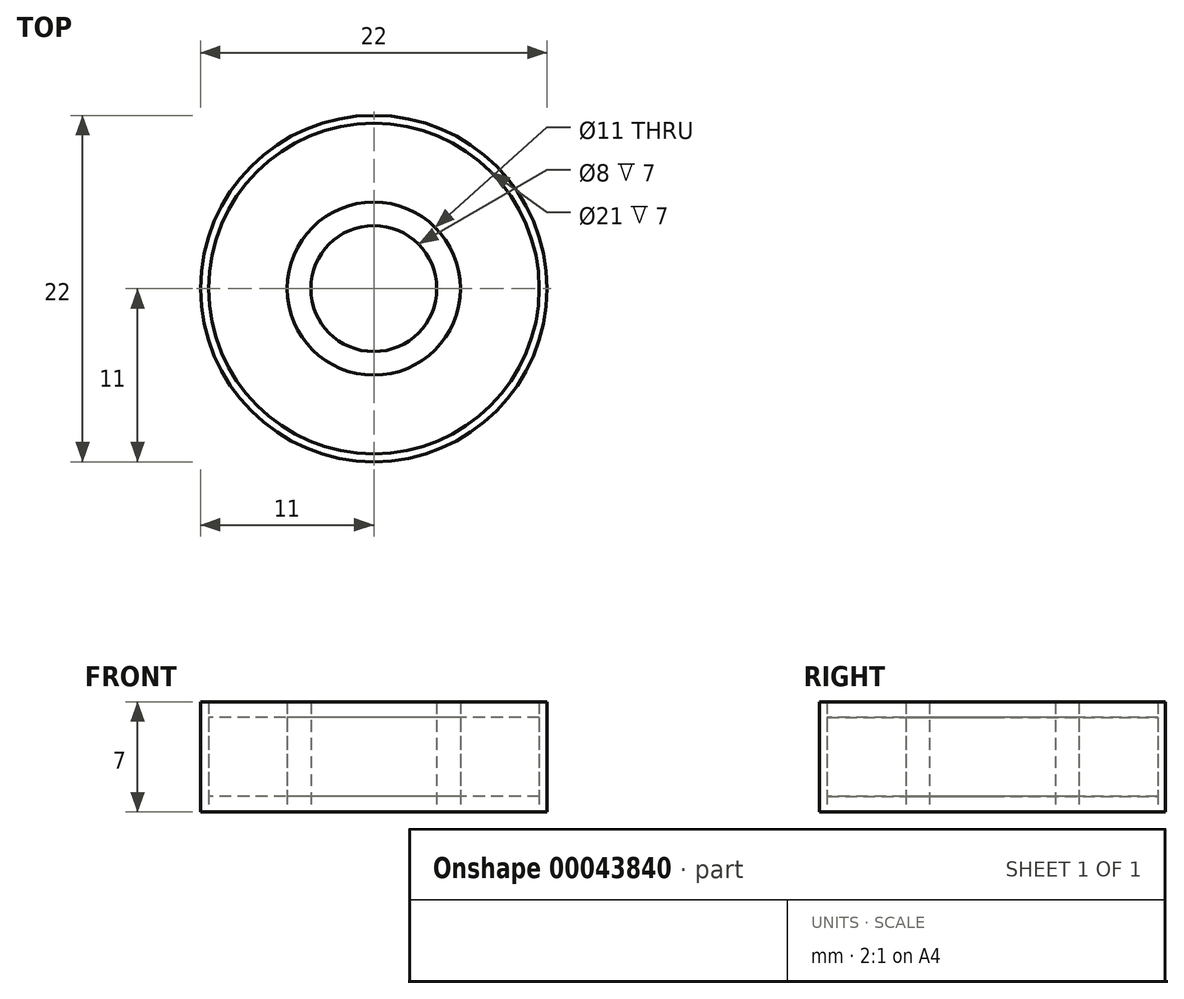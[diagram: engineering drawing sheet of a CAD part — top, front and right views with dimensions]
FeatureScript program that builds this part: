
annotation { "Feature Type Name" : "Feature", "Feature Type Description" : "" }
export const myFeature = defineFeature(function(context is Context, id is Id, definition is map)
    precondition{}
    {
        {
            var Q0;
            Q0=qCreatedBy(makeId("Top.planeOp"),FACE);
            var sketch = newSketch(context, id + "F0", { "sketchPlane" : qUnion([Q0])});
            skCircle(sketch, "E0", {"center": v(0, 0) * mm, "radius": 4 * mm});
            skCircle(sketch, "E1", {"center": v(0, 0) * mm, "radius": 11 * mm});
            skCircle(sketch, "E2", {"center": v(0, 0) * mm, "radius": 5.5 * mm});
            skCircle(sketch, "E3", {"center": v(0, 0) * mm, "radius": 10.5 * mm});
            skSolve(sketch);
        }
        {
            var Q0;
            Q0=makeQuery(id+"F0.imprint","IMPRINT",FACE,{"disambiguationData":[TD([[makeQuery(id+"F0.imprint","IMPRINT",EDGE,{"derivedFrom":sQuery(id+"F0.wireOp",EDGE,"E0")}),-1.0]])]});
            var Q1;
            Q1=makeQuery(id+"F0.imprint","IMPRINT",FACE,{"disambiguationData":[TD([[makeQuery(id+"F0.imprint","IMPRINT",EDGE,{"derivedFrom":sQuery(id+"F0.wireOp",EDGE,"E1")}),1.0]])]});
            extrude(context, id + "F1", {"entities" : qUnion([Q0, Q1]), "depth" : 7 * mm});
        }
        {
            var Q0;
            Q0=makeQuery(id+"F0.imprint","IMPRINT",FACE,{"disambiguationData":[TD([[makeQuery(id+"F0.imprint","IMPRINT",EDGE,{"derivedFrom":sQuery(id+"F0.wireOp",EDGE,"E2")}),-1.0]])]});
            extrude(context, id + "F2", {"entities" : qUnion([Q0]), "depth" : 5 * mm});
        }
        {
            var Q0;
            Q0=makeQuery(id+"F2.opExtrude","SWEPT_BODY",BODY,{"disambiguationData":[OSD([sQuery(id+"F0.wireOp",EDGE,"E2"),sQuery(id+"F0.wireOp",EDGE,"E3")])]});
            transform(context, id + "F3", {"entities" : qUnion([Q0]), "transformType" : TransformType.TRANSLATION_3D, "dx" : 0 * mm, "dy" : 0 * mm, "dz" : 1 * mm, "makeCopy" : false});
        }
    });
